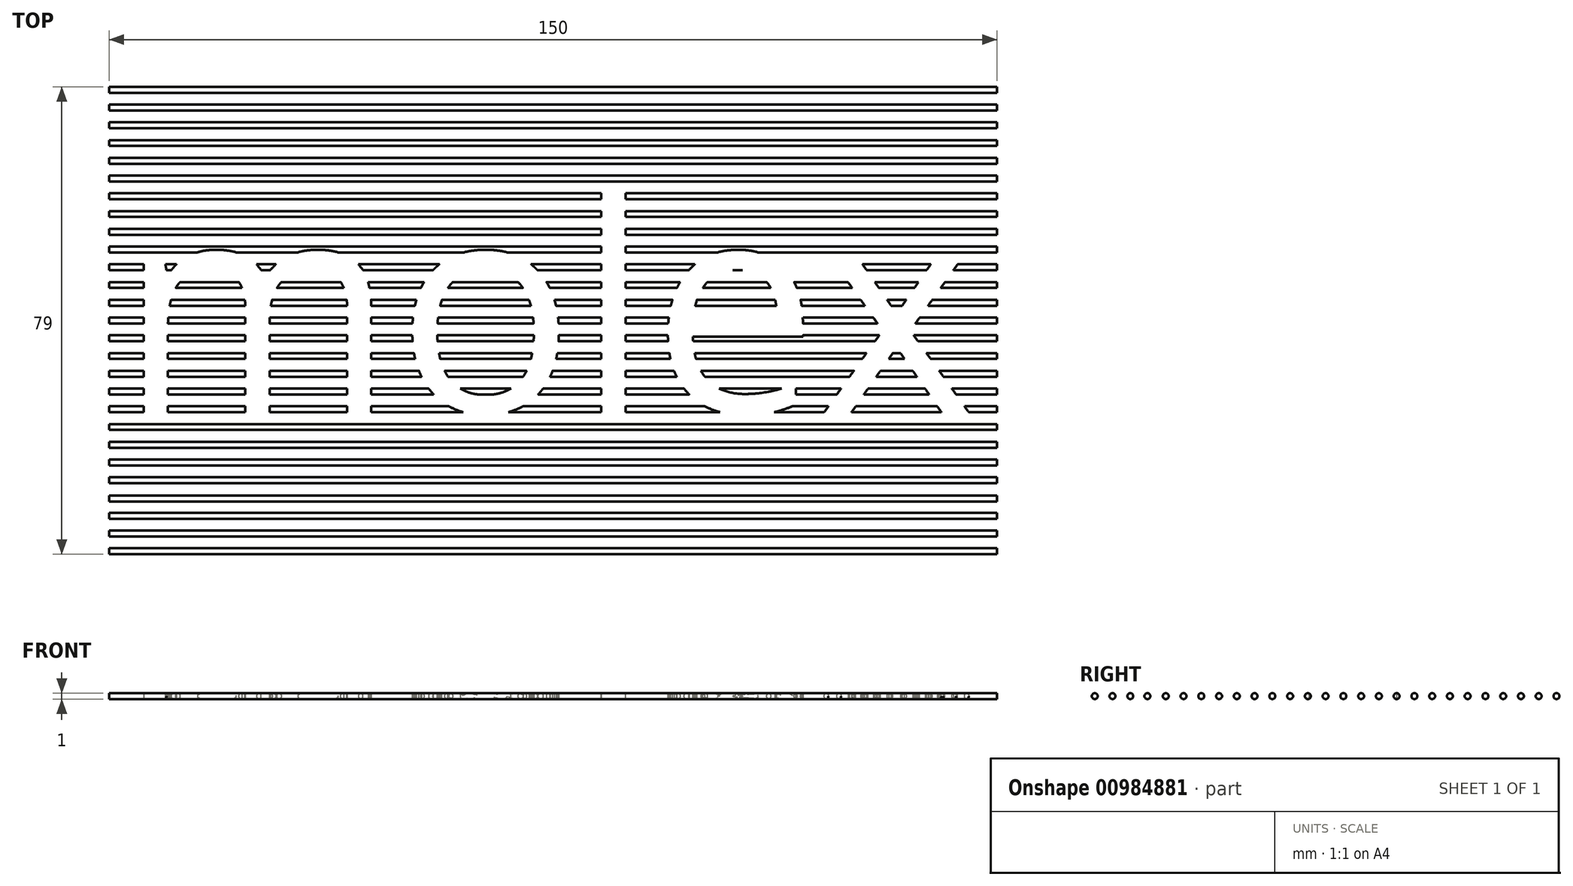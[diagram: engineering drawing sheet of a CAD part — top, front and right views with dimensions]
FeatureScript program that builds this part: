
annotation { "Feature Type Name" : "Feature", "Feature Type Description" : "" }
export const myFeature = defineFeature(function(context is Context, id is Id, definition is map)
    precondition{}
    {
        {
            var Q0;
            Q0=qCreatedBy(makeId("Top.planeOp"),FACE);
            var sketch = newSketch(context, id + "F0", { "sketchPlane" : qUnion([Q0])});
            skLineSegment(sketch, "E0", {"start": v(-75, 57.1) * mm, "end": v(75, 57.1) * mm});
            skLineSegment(sketch, "E1", {"start": v(-75, 39.1) * mm, "end": v(75, 39.1) * mm});
            skLineSegment(sketch, "E2", {"start": v(-75, 36.1) * mm, "end": v(75, 36.1) * mm});
            skLineSegment(sketch, "E3", {"start": v(-75, 51.1) * mm, "end": v(75, 51.1) * mm});
            skLineSegment(sketch, "E4", {"start": v(-75, 42.1) * mm, "end": v(75, 42.1) * mm});
            skLineSegment(sketch, "E5", {"start": v(-75, 33.1) * mm, "end": v(75, 33.1) * mm});
            skLineSegment(sketch, "E6", {"start": v(-75, 30.1) * mm, "end": v(75, 30.1) * mm});
            skLineSegment(sketch, "E7", {"start": v(-75, 27.1) * mm, "end": v(75, 27.1) * mm});
            skLineSegment(sketch, "E8", {"start": v(-75, 24.1) * mm, "end": v(75, 24.1) * mm});
            skLineSegment(sketch, "E9", {"start": v(-75, 21.1) * mm, "end": v(75, 21.1) * mm});
            skLineSegment(sketch, "E10", {"start": v(-75, 18.1) * mm, "end": v(75, 18.1) * mm});
            skLineSegment(sketch, "E11", {"start": v(-75, 15.1) * mm, "end": v(75, 15.1) * mm});
            skLineSegment(sketch, "E12", {"start": v(-75, 12.1) * mm, "end": v(75, 12.1) * mm});
            skLineSegment(sketch, "E13", {"start": v(-75, 9.1) * mm, "end": v(75, 9.1) * mm});
            skLineSegment(sketch, "E14", {"start": v(-75, 6.1) * mm, "end": v(75, 6.1) * mm});
            skLineSegment(sketch, "E15", {"start": v(-75, 0.1) * mm, "end": v(75, 0.1) * mm});
            skLineSegment(sketch, "E16", {"start": v(-75, -2.9) * mm, "end": v(75, -2.9) * mm});
            skLineSegment(sketch, "E17", {"start": v(-75, -8.9) * mm, "end": v(75, -8.9) * mm});
            skLineSegment(sketch, "E18", {"start": v(-75, -5.9) * mm, "end": v(75, -5.9) * mm});
            skLineSegment(sketch, "E19", {"start": v(-75, 3.1) * mm, "end": v(75, 3.1) * mm});
            skLineSegment(sketch, "E20", {"start": v(-75, 63.1) * mm, "end": v(75, 63.1) * mm});
            skLineSegment(sketch, "E21", {"start": v(-75, 66.1) * mm, "end": v(75, 66.1) * mm});
            skLineSegment(sketch, "E22", {"start": v(-75, 69.1) * mm, "end": v(75, 69.1) * mm});
            skLineSegment(sketch, "E23", {"start": v(-75, 45.1) * mm, "end": v(75, 45.1) * mm});
            skLineSegment(sketch, "E24", {"start": v(-75, 60.1) * mm, "end": v(75, 60.1) * mm});
            skLineSegment(sketch, "E25", {"start": v(-75, 54.1) * mm, "end": v(75, 54.1) * mm});
            skLineSegment(sketch, "E26", {"start": v(-75, 48.1) * mm, "end": v(75, 48.1) * mm});
            skPoint(sketch, "E27", {"position": v(0, 69.1) * mm});
            skPoint(sketch, "E28", {"position": v(-75, 36.1) * mm});
            skPoint(sketch, "E29", {"position": v(-75, 33.1) * mm});
            skPoint(sketch, "E30", {"position": v(-75, 30.1) * mm});
            skPoint(sketch, "E31", {"position": v(-75, 27.1) * mm});
            skPoint(sketch, "E32", {"position": v(-75, 24.1) * mm});
            skPoint(sketch, "E33", {"position": v(-75, 21.1) * mm});
            skPoint(sketch, "E34", {"position": v(-75, 18.1) * mm});
            skPoint(sketch, "E35", {"position": v(-75, 15.1) * mm});
            skPoint(sketch, "E36", {"position": v(-75, 12.1) * mm});
            skPoint(sketch, "E37", {"position": v(-75, 9.1) * mm});
            skPoint(sketch, "E38", {"position": v(-75, 6.1) * mm});
            skPoint(sketch, "E39", {"position": v(-75, 3.1) * mm});
            skPoint(sketch, "E40", {"position": v(-75, 0.1) * mm});
            skPoint(sketch, "E41", {"position": v(-75, -2.9) * mm});
            skPoint(sketch, "E42", {"position": v(-75, -5.9) * mm});
            skPoint(sketch, "E43", {"position": v(-75, -8.9) * mm});
            skPoint(sketch, "E44", {"position": v(-75, 39.1) * mm});
            skPoint(sketch, "E45", {"position": v(-75, 42.1) * mm});
            skPoint(sketch, "E46", {"position": v(-75, 45.1) * mm});
            skPoint(sketch, "E47", {"position": v(-75, 48.1) * mm});
            skPoint(sketch, "E48", {"position": v(-75, 51.1) * mm});
            skPoint(sketch, "E49", {"position": v(-75, 54.1) * mm});
            skPoint(sketch, "E50", {"position": v(-75, 57.1) * mm});
            skPoint(sketch, "E51", {"position": v(-75, 60.1) * mm});
            skPoint(sketch, "E52", {"position": v(-75, 63.1) * mm});
            skPoint(sketch, "E53", {"position": v(-75, 66.1) * mm});
            skPoint(sketch, "E54", {"position": v(-75, 69.1) * mm});
            skSolve(sketch);
        }
        {
            var Q0;
            Q0=qCreatedBy(makeId("Right.planeOp"),FACE);
            var sketch = newSketch(context, id + "F1", { "sketchPlane" : qUnion([Q0])});
            skPoint(sketch, "E55.0", {"position": v(69.1, 0) * mm});
            skPoint(sketch, "E56.0", {"position": v(66.1, 0) * mm});
            skPoint(sketch, "E57.0", {"position": v(63.1, 0) * mm});
            skPoint(sketch, "E58.0", {"position": v(60.1, 0) * mm});
            skPoint(sketch, "E59.0", {"position": v(57.1, 0) * mm});
            skPoint(sketch, "E60.0", {"position": v(54.1, 0) * mm});
            skPoint(sketch, "E61.0", {"position": v(51.1, 0) * mm});
            skPoint(sketch, "E62.0", {"position": v(48.1, 0) * mm});
            skPoint(sketch, "E63.0", {"position": v(45.1, 0) * mm});
            skPoint(sketch, "E64.0", {"position": v(42.1, 0) * mm});
            skPoint(sketch, "E65.0", {"position": v(39.1, 0) * mm});
            skPoint(sketch, "E66.0", {"position": v(36.1, 0) * mm});
            skPoint(sketch, "E67.0", {"position": v(33.1, 0) * mm});
            skPoint(sketch, "E68.0", {"position": v(30.1, 0) * mm});
            skPoint(sketch, "E69.0", {"position": v(27.1, 0) * mm});
            skPoint(sketch, "E70.0", {"position": v(24.1, 0) * mm});
            skPoint(sketch, "E71.0", {"position": v(21.1, 0) * mm});
            skPoint(sketch, "E72.0", {"position": v(18.1, 0) * mm});
            skPoint(sketch, "E73.0", {"position": v(15.1, 0) * mm});
            skPoint(sketch, "E74.0", {"position": v(9.1, 0) * mm});
            skPoint(sketch, "E75.0", {"position": v(6.1, 0) * mm});
            skPoint(sketch, "E76.0", {"position": v(3.1, 0) * mm});
            skPoint(sketch, "E77.0", {"position": v(12.1, 0) * mm});
            skPoint(sketch, "E78.0", {"position": v(-2.9, 0) * mm});
            skPoint(sketch, "E79.0", {"position": v(-5.9, 0) * mm});
            skPoint(sketch, "E80.0", {"position": v(-8.9, 0) * mm});
            skPoint(sketch, "E81.0", {"position": v(0.1, 0) * mm});
            skCircle(sketch, "E82", {"center": v(-8.9, 0) * mm, "radius": 0.5 * mm});
            skCircle(sketch, "E83", {"center": v(-5.9, 0) * mm, "radius": 0.5 * mm});
            skCircle(sketch, "E84", {"center": v(-2.9, 0) * mm, "radius": 0.5 * mm});
            skCircle(sketch, "E85", {"center": v(0, 0) * mm, "radius": 0.5 * mm});
            skCircle(sketch, "E86", {"center": v(3.1, 0) * mm, "radius": 0.5 * mm});
            skCircle(sketch, "E87", {"center": v(6.1, 0) * mm, "radius": 0.5 * mm});
            skCircle(sketch, "E88", {"center": v(9.1, 0) * mm, "radius": 0.5 * mm});
            skCircle(sketch, "E89", {"center": v(12.1, 0) * mm, "radius": 0.5 * mm});
            skCircle(sketch, "E90", {"center": v(15.1, 0) * mm, "radius": 0.5 * mm});
            skCircle(sketch, "E91", {"center": v(18.1, 0) * mm, "radius": 0.5 * mm});
            skCircle(sketch, "E92", {"center": v(21.1, 0) * mm, "radius": 0.5 * mm});
            skCircle(sketch, "E93", {"center": v(24.1, 0) * mm, "radius": 0.5 * mm});
            skCircle(sketch, "E94", {"center": v(27.1, 0) * mm, "radius": 0.5 * mm});
            skCircle(sketch, "E95", {"center": v(30.1, 0) * mm, "radius": 0.5 * mm});
            skCircle(sketch, "E96", {"center": v(33.1, 0) * mm, "radius": 0.5 * mm});
            skCircle(sketch, "E97", {"center": v(36.1, 0) * mm, "radius": 0.5 * mm});
            skCircle(sketch, "E98", {"center": v(39.1, 0) * mm, "radius": 0.5 * mm});
            skCircle(sketch, "E99", {"center": v(42.1, 0) * mm, "radius": 0.5 * mm});
            skCircle(sketch, "E100", {"center": v(45.1, 0) * mm, "radius": 0.5 * mm});
            skCircle(sketch, "E101", {"center": v(48.1, 0) * mm, "radius": 0.5 * mm});
            skCircle(sketch, "E102", {"center": v(51.1, 0) * mm, "radius": 0.5 * mm});
            skCircle(sketch, "E103", {"center": v(54.1, 0) * mm, "radius": 0.5 * mm});
            skCircle(sketch, "E104", {"center": v(57.1, 0) * mm, "radius": 0.5 * mm});
            skCircle(sketch, "E105", {"center": v(60.1, 0) * mm, "radius": 0.5 * mm});
            skCircle(sketch, "E106", {"center": v(63.1, 0) * mm, "radius": 0.5 * mm});
            skCircle(sketch, "E107", {"center": v(66.1, 0) * mm, "radius": 0.5 * mm});
            skCircle(sketch, "E108", {"center": v(69.1, 0) * mm, "radius": 0.5 * mm});
            skSolve(sketch);
        }
        {
            var Q0;
            Q0=makeQuery(id+"F1.imprint","IMPRINT",FACE,{"disambiguationData":[TD([[makeQuery(id+"F1.imprint","IMPRINT",EDGE,{"derivedFrom":sQuery(id+"F1.wireOp",EDGE,"E108")}),1.0]])]});
            var Q1;
            Q1=makeQuery(id+"F1.imprint","IMPRINT",FACE,{"disambiguationData":[TD([[makeQuery(id+"F1.imprint","IMPRINT",EDGE,{"derivedFrom":sQuery(id+"F1.wireOp",EDGE,"E107")}),1.0]])]});
            var Q2;
            Q2=makeQuery(id+"F1.imprint","IMPRINT",FACE,{"disambiguationData":[TD([[makeQuery(id+"F1.imprint","IMPRINT",EDGE,{"derivedFrom":sQuery(id+"F1.wireOp",EDGE,"E106")}),1.0]])]});
            var Q3;
            Q3=makeQuery(id+"F1.imprint","IMPRINT",FACE,{"disambiguationData":[TD([[makeQuery(id+"F1.imprint","IMPRINT",EDGE,{"derivedFrom":sQuery(id+"F1.wireOp",EDGE,"E105")}),1.0]])]});
            var Q4;
            Q4=makeQuery(id+"F1.imprint","IMPRINT",FACE,{"disambiguationData":[TD([[makeQuery(id+"F1.imprint","IMPRINT",EDGE,{"derivedFrom":sQuery(id+"F1.wireOp",EDGE,"E104")}),1.0]])]});
            var Q5;
            Q5=makeQuery(id+"F1.imprint","IMPRINT",FACE,{"disambiguationData":[TD([[makeQuery(id+"F1.imprint","IMPRINT",EDGE,{"derivedFrom":sQuery(id+"F1.wireOp",EDGE,"E103")}),1.0]])]});
            var Q6;
            Q6=makeQuery(id+"F1.imprint","IMPRINT",FACE,{"disambiguationData":[TD([[makeQuery(id+"F1.imprint","IMPRINT",EDGE,{"derivedFrom":sQuery(id+"F1.wireOp",EDGE,"E102")}),1.0]])]});
            var Q7;
            Q7=makeQuery(id+"F1.imprint","IMPRINT",FACE,{"disambiguationData":[TD([[makeQuery(id+"F1.imprint","IMPRINT",EDGE,{"derivedFrom":sQuery(id+"F1.wireOp",EDGE,"E101")}),1.0]])]});
            var Q8;
            Q8=makeQuery(id+"F1.imprint","IMPRINT",FACE,{"disambiguationData":[TD([[makeQuery(id+"F1.imprint","IMPRINT",EDGE,{"derivedFrom":sQuery(id+"F1.wireOp",EDGE,"E100")}),1.0]])]});
            var Q9;
            Q9=makeQuery(id+"F1.imprint","IMPRINT",FACE,{"disambiguationData":[TD([[makeQuery(id+"F1.imprint","IMPRINT",EDGE,{"derivedFrom":sQuery(id+"F1.wireOp",EDGE,"E99")}),1.0]])]});
            var Q10;
            Q10=makeQuery(id+"F1.imprint","IMPRINT",FACE,{"disambiguationData":[TD([[makeQuery(id+"F1.imprint","IMPRINT",EDGE,{"derivedFrom":sQuery(id+"F1.wireOp",EDGE,"E98")}),1.0]])]});
            var Q11;
            Q11=makeQuery(id+"F1.imprint","IMPRINT",FACE,{"disambiguationData":[TD([[makeQuery(id+"F1.imprint","IMPRINT",EDGE,{"derivedFrom":sQuery(id+"F1.wireOp",EDGE,"E97")}),1.0]])]});
            var Q12;
            Q12=makeQuery(id+"F1.imprint","IMPRINT",FACE,{"disambiguationData":[TD([[makeQuery(id+"F1.imprint","IMPRINT",EDGE,{"derivedFrom":sQuery(id+"F1.wireOp",EDGE,"E96")}),1.0]])]});
            var Q13;
            Q13=makeQuery(id+"F1.imprint","IMPRINT",FACE,{"disambiguationData":[TD([[makeQuery(id+"F1.imprint","IMPRINT",EDGE,{"derivedFrom":sQuery(id+"F1.wireOp",EDGE,"E95")}),1.0]])]});
            var Q14;
            Q14=makeQuery(id+"F1.imprint","IMPRINT",FACE,{"disambiguationData":[TD([[makeQuery(id+"F1.imprint","IMPRINT",EDGE,{"derivedFrom":sQuery(id+"F1.wireOp",EDGE,"E94")}),1.0]])]});
            var Q15;
            Q15=makeQuery(id+"F1.imprint","IMPRINT",FACE,{"disambiguationData":[TD([[makeQuery(id+"F1.imprint","IMPRINT",EDGE,{"derivedFrom":sQuery(id+"F1.wireOp",EDGE,"E93")}),1.0]])]});
            var Q16;
            Q16=makeQuery(id+"F1.imprint","IMPRINT",FACE,{"disambiguationData":[TD([[makeQuery(id+"F1.imprint","IMPRINT",EDGE,{"derivedFrom":sQuery(id+"F1.wireOp",EDGE,"E92")}),1.0]])]});
            var Q17;
            Q17=makeQuery(id+"F1.imprint","IMPRINT",FACE,{"disambiguationData":[TD([[makeQuery(id+"F1.imprint","IMPRINT",EDGE,{"derivedFrom":sQuery(id+"F1.wireOp",EDGE,"E91")}),1.0]])]});
            var Q18;
            Q18=makeQuery(id+"F1.imprint","IMPRINT",FACE,{"disambiguationData":[TD([[makeQuery(id+"F1.imprint","IMPRINT",EDGE,{"derivedFrom":sQuery(id+"F1.wireOp",EDGE,"E90")}),1.0]])]});
            var Q19;
            Q19=makeQuery(id+"F1.imprint","IMPRINT",FACE,{"disambiguationData":[TD([[makeQuery(id+"F1.imprint","IMPRINT",EDGE,{"derivedFrom":sQuery(id+"F1.wireOp",EDGE,"E89")}),1.0]])]});
            var Q20;
            Q20=makeQuery(id+"F1.imprint","IMPRINT",FACE,{"disambiguationData":[TD([[makeQuery(id+"F1.imprint","IMPRINT",EDGE,{"derivedFrom":sQuery(id+"F1.wireOp",EDGE,"E87")}),1.0]])]});
            var Q21;
            Q21=makeQuery(id+"F1.imprint","IMPRINT",FACE,{"disambiguationData":[TD([[makeQuery(id+"F1.imprint","IMPRINT",EDGE,{"derivedFrom":sQuery(id+"F1.wireOp",EDGE,"E86")}),1.0]])]});
            var Q22;
            Q22=makeQuery(id+"F1.imprint","IMPRINT",FACE,{"disambiguationData":[TD([[makeQuery(id+"F1.imprint","IMPRINT",EDGE,{"derivedFrom":sQuery(id+"F1.wireOp",EDGE,"E82")}),1.0]])]});
            var Q23;
            Q23=makeQuery(id+"F1.imprint","IMPRINT",FACE,{"disambiguationData":[TD([[makeQuery(id+"F1.imprint","IMPRINT",EDGE,{"derivedFrom":sQuery(id+"F1.wireOp",EDGE,"E83")}),1.0]])]});
            var Q24;
            Q24=makeQuery(id+"F1.imprint","IMPRINT",FACE,{"disambiguationData":[TD([[makeQuery(id+"F1.imprint","IMPRINT",EDGE,{"derivedFrom":sQuery(id+"F1.wireOp",EDGE,"E84")}),1.0]])]});
            var Q25;
            Q25=makeQuery(id+"F1.imprint","IMPRINT",FACE,{"disambiguationData":[TD([[makeQuery(id+"F1.imprint","IMPRINT",EDGE,{"derivedFrom":sQuery(id+"F1.wireOp",EDGE,"E85")}),1.0]])]});
            var Q26;
            Q26=makeQuery(id+"F1.imprint","IMPRINT",FACE,{"disambiguationData":[TD([[makeQuery(id+"F1.imprint","IMPRINT",EDGE,{"derivedFrom":sQuery(id+"F1.wireOp",EDGE,"E88")}),1.0]])]});
            var Q27;
            Q27=sQuery(id+"F0.wireOp",EDGE,"E22");
            sweep(context, id + "F2", {"profiles" : qUnion([Q0, Q1, Q2, Q3, Q4, Q5, Q6, Q7, Q8, Q9, Q10, Q11, Q12, Q13, Q14, Q15, Q16, Q17, Q18, Q19, Q20, Q21, Q22, Q23, Q24, Q25, Q26]), "path" : qUnion([Q27])});
        }
        {
            var Q0;
            Q0=qCreatedBy(makeId("Top.planeOp"),FACE);
            var sketch = newSketch(context, id + "F3", { "sketchPlane" : qUnion([Q0])});
            skText(sketch, "E109", { "text": "molex", "fontName": "OpenSans-Regular.ttf"});
            skLineSegment(sketch, "E110", {"start": v(-75, 69.6) * mm, "end": v(75, 69.6) * mm});
            skLineSegment(sketch, "E111", {"start": v(75, -9.4) * mm, "end": v(-75, -9.4) * mm});
            const initialGuessF3  = {"E109": [-0.0735, 0.0146, 1, 0, 0.03628]};
            skSetInitialGuess(sketch, initialGuessF3);
            skSolve(sketch);
        }
        {
            var Q0;
            Q0 = qSketchRegion(id + "F3", true);
            extrude(context, id + "F4", {"entities" : qUnion([Q0]), "operationType" : NewBodyOperationType.REMOVE, "endBound" : BoundingType.SYMMETRIC, "depth" : 35 * mm, "offsetDistance" : 25 * mm});
        }
    });
